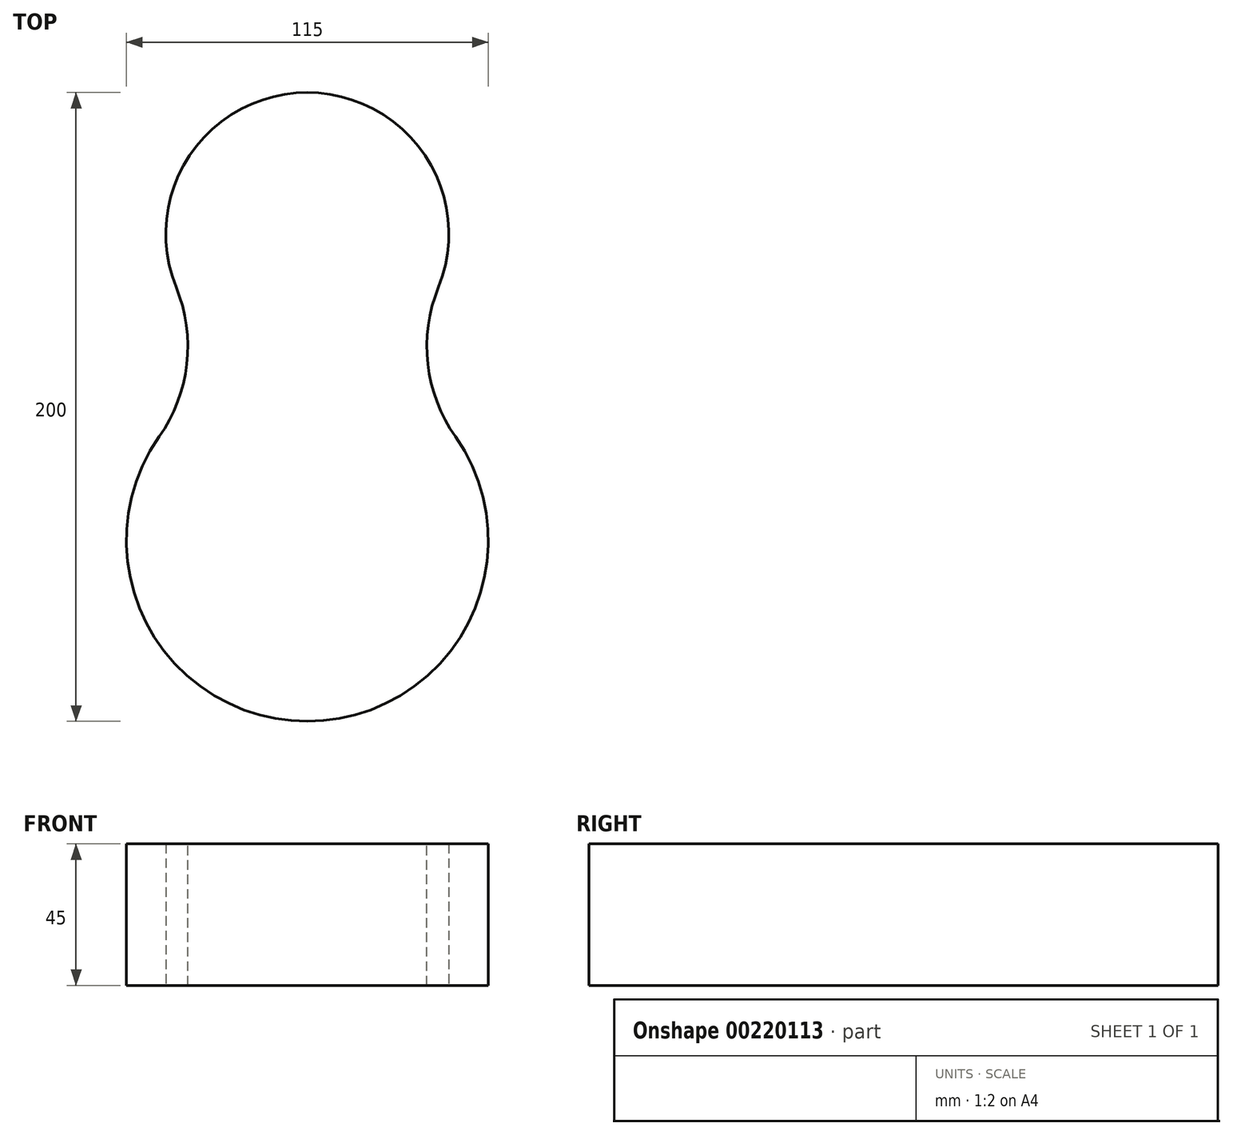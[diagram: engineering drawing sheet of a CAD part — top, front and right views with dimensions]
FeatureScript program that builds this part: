
annotation { "Feature Type Name" : "Feature", "Feature Type Description" : "" }
export const myFeature = defineFeature(function(context is Context, id is Id, definition is map)
    precondition{}
    {
        {
            var Q0;
            Q0=qCreatedBy(makeId("Top.planeOp"),FACE);
            var sketch = newSketch(context, id + "F0", { "sketchPlane" : qUnion([Q0])});
            skLineSegment(sketch, "E0.bottom", {"start": v(57.5, -100) * mm, "end": v(-57.5, -100) * mm, "construction": true});
            skLineSegment(sketch, "E0.top", {"start": v(57.5, 100) * mm, "end": v(-57.5, 100) * mm, "construction": true});
            skLineSegment(sketch, "E0.left", {"start": v(57.5, -100) * mm, "end": v(57.5, 100) * mm, "construction": true});
            skLineSegment(sketch, "E0.right", {"start": v(-57.5, -100) * mm, "end": v(-57.5, 100) * mm, "construction": true});
            skPoint(sketch, "E0.middle", {"position": v(0, 0) * mm});
            skLineSegment(sketch, "E1", {"start": v(0, 100) * mm, "end": v(0, -100) * mm, "construction": true});
            skArc(sketch, "E2", {"start": v(38.59, 31.85) * mm, "mid": v(0, 100) * mm, "end": v(-38.59, 31.85) * mm});
            skArc(sketch, "E3", {"start": v(-46.33, -8.45) * mm, "mid": v(0, -100) * mm, "end": v(46.33, -8.45) * mm});
            skArc(sketch, "E4", {"start": v(-47.5, -10.08) * mm, "mid": v(-38.5, 9.92) * mm, "end": v(-38.59, 31.85) * mm});
            skArc(sketch, "E5.MirrorCS", {"start": v(47.5, -10.08) * mm, "mid": v(38.5, 9.92) * mm, "end": v(38.59, 31.85) * mm});
            skSolve(sketch);
        }
        {
            var Q0;
            Q0 = qSketchRegion(id + "F0", true);
            extrude(context, id + "F1", {"entities" : qUnion([Q0]), "depth" : 45 * mm});
        }
        {
            var Q0;
            Q0=makeQuery(id+"F1.opExtrude","SWEPT_EDGE",EDGE,{"disambiguationData":[OSD([sQuery(id+"F0.wireOp",EDGE,"E2"),sQuery(id+"F0.wireOp",EDGE,"E4")])]});
            var Q1;
            Q1=makeQuery(id+"F1.opExtrude","SWEPT_EDGE",EDGE,{"disambiguationData":[OSD([sQuery(id+"F0.wireOp",EDGE,"E2"),sQuery(id+"F0.wireOp",EDGE,"E5.MirrorCS")])]});
            fillet(context, id + "F2", {"entities" : qUnion([Q0, Q1]), "radius" : 50 * mm, "tangentPropagation" : true, "allowEdgeOverflow" : false});
        }
    });
